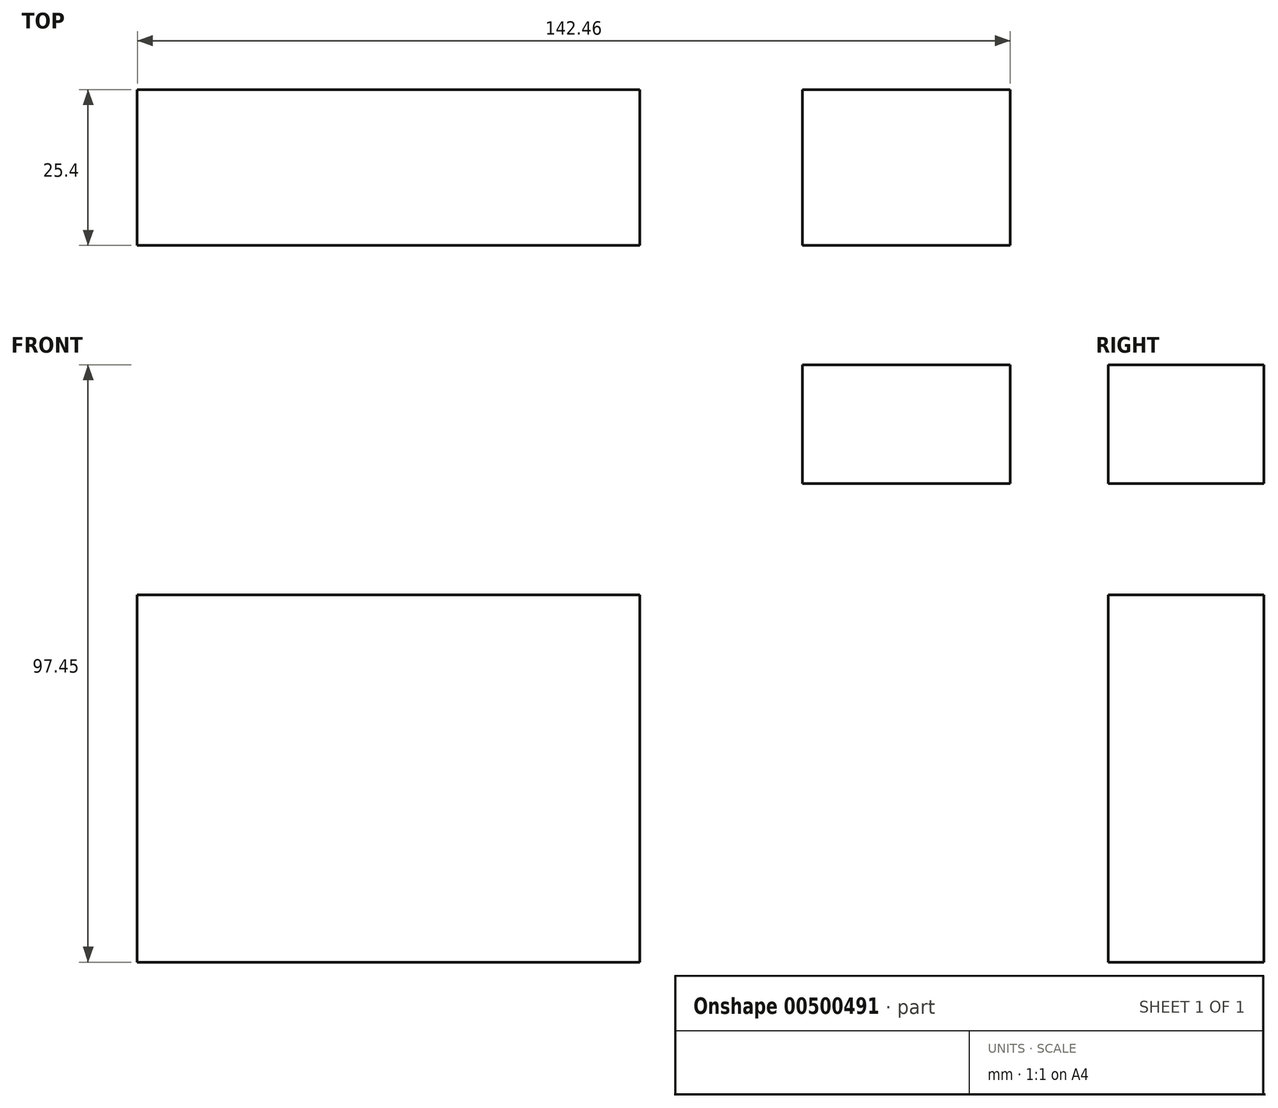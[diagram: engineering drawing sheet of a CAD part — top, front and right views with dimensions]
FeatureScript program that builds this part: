
annotation { "Feature Type Name" : "Feature", "Feature Type Description" : "" }
export const myFeature = defineFeature(function(context is Context, id is Id, definition is map)
    precondition{}
    {
        {
            var Q0;
            Q0=qCreatedBy(makeId("Front.planeOp"),FACE);
            var sketch = newSketch(context, id + "F0", { "sketchPlane" : qUnion([Q0])});
            skLineSegment(sketch, "E0.bottom", {"start": v(-41.76, 29.2) * mm, "end": v(40.22, 29.2) * mm});
            skLineSegment(sketch, "E0.top", {"start": v(-41.76, -30.74) * mm, "end": v(40.22, -30.74) * mm});
            skLineSegment(sketch, "E0.left", {"start": v(-41.76, 29.2) * mm, "end": v(-41.76, -30.74) * mm});
            skLineSegment(sketch, "E0.right", {"start": v(40.22, 29.2) * mm, "end": v(40.22, -30.74) * mm});
            skLineSegment(sketch, "E1.bottom", {"start": v(66.78, 66.7) * mm, "end": v(100.7, 66.7) * mm});
            skLineSegment(sketch, "E1.top", {"start": v(66.78, 47.37) * mm, "end": v(100.7, 47.37) * mm});
            skLineSegment(sketch, "E1.left", {"start": v(66.78, 66.7) * mm, "end": v(66.78, 47.37) * mm});
            skLineSegment(sketch, "E1.right", {"start": v(100.7, 66.7) * mm, "end": v(100.7, 47.37) * mm});
            skFitSpline(sketch, "E2", {"points": [v(26.3, 24.17) * mm, v(26.3, 47.37) * mm], "startDerivative": vector(0, 23.2) * mm, "endDerivative": vector(0, 23.2) * mm, "construction": true});
            skSolve(sketch);
        }
        {
            var Q0;
            Q0 = qSketchRegion(id + "F0", true);
            extrude(context, id + "F1", {"entities" : qUnion([Q0]), "depth" : 25.4 * mm});
        }
    });
